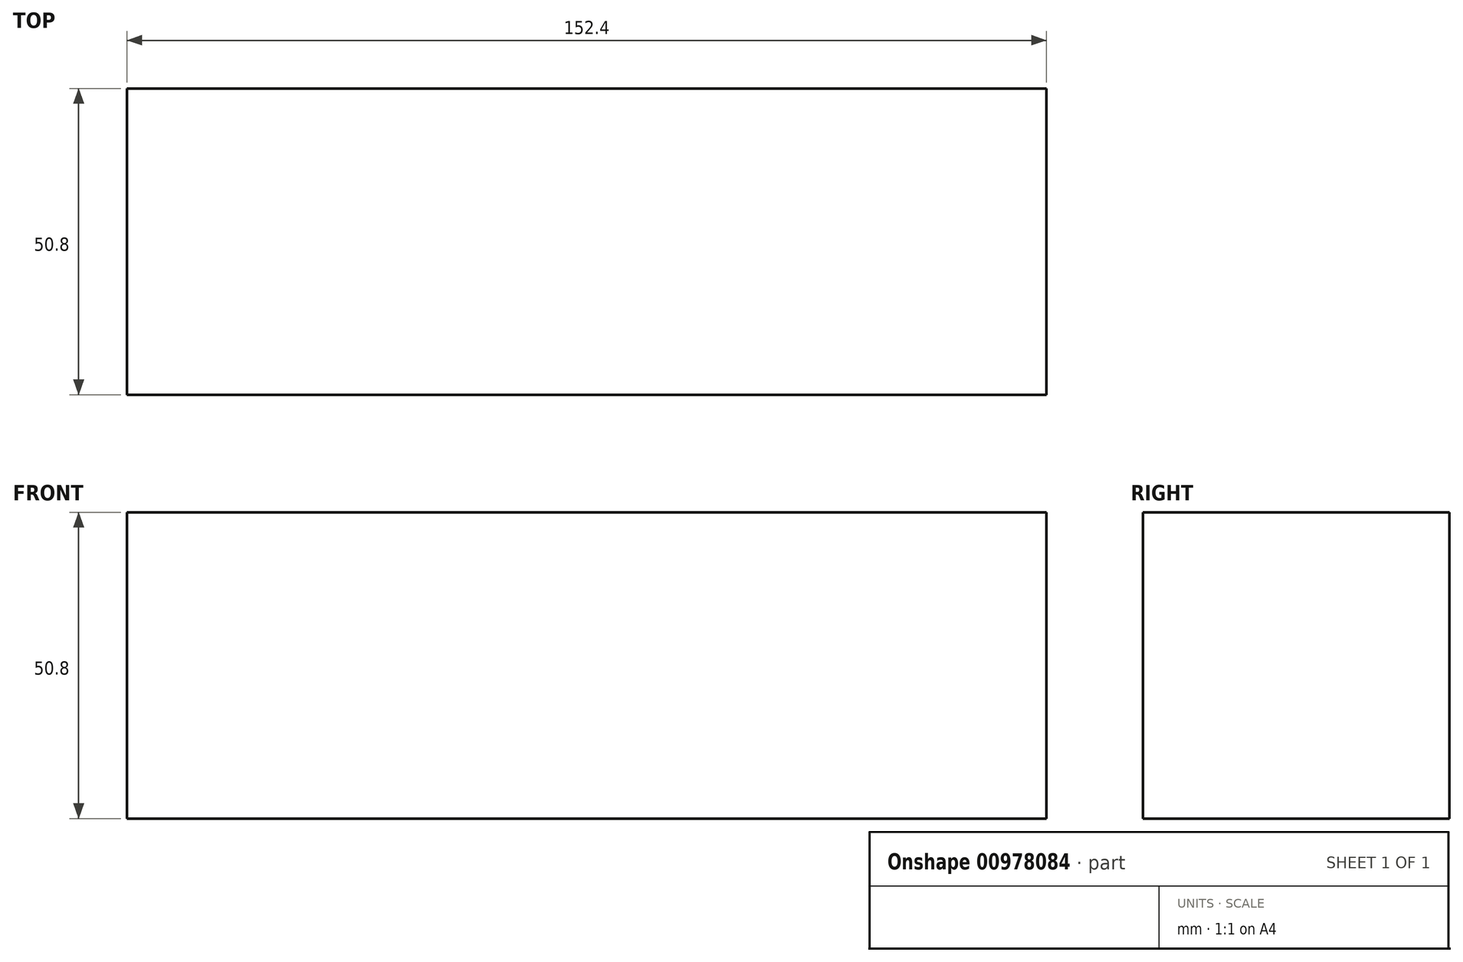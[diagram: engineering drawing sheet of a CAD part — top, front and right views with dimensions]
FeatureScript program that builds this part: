
annotation { "Feature Type Name" : "Feature", "Feature Type Description" : "" }
export const myFeature = defineFeature(function(context is Context, id is Id, definition is map)
    precondition{}
    {
        {
            var Q0;
            Q0=qCreatedBy(makeId("Front.planeOp"),FACE);
            var sketch = newSketch(context, id + "F0", { "sketchPlane" : qUnion([Q0])});
            skLineSegment(sketch, "E0.bottom", {"start": v(0, 0) * mm, "end": v(152.4, 0) * mm});
            skLineSegment(sketch, "E0.top", {"start": v(0, 50.8) * mm, "end": v(152.4, 50.8) * mm});
            skLineSegment(sketch, "E0.left", {"start": v(0, 0) * mm, "end": v(0, 50.8) * mm});
            skLineSegment(sketch, "E0.right", {"start": v(152.4, 0) * mm, "end": v(152.4, 50.8) * mm});
            skSolve(sketch);
        }
        {
            var Q0;
            Q0 = qSketchRegion(id + "F0", true);
            extrude(context, id + "F1", {"entities" : qUnion([Q0]), "depth" : 50.8 * mm, "offsetDistance" : 25.4 * mm});
        }
    });
